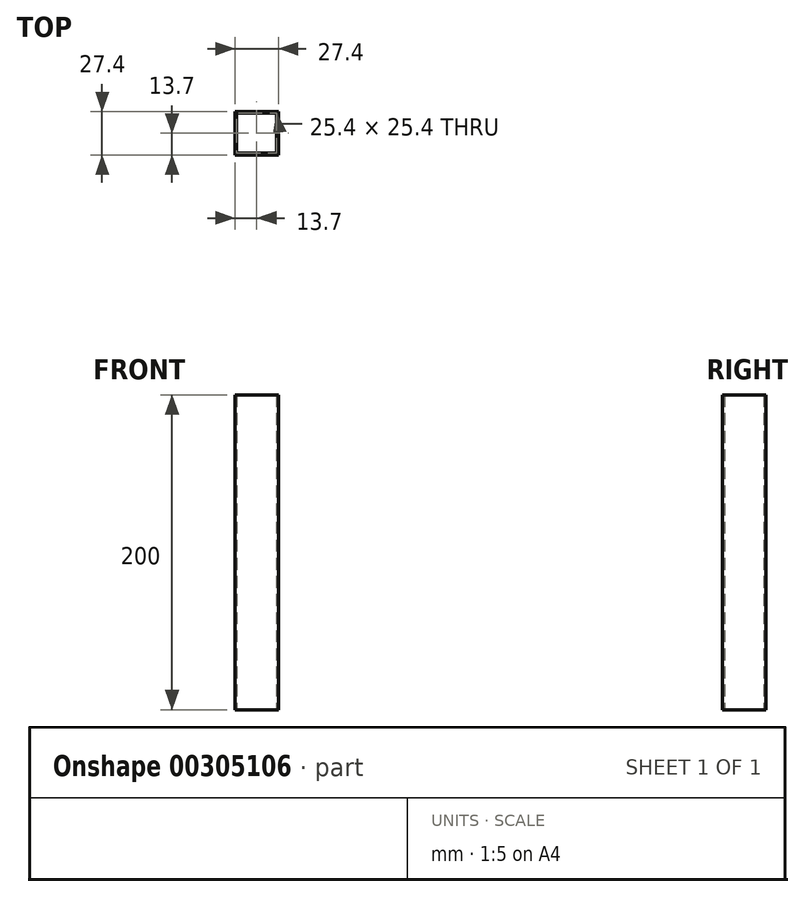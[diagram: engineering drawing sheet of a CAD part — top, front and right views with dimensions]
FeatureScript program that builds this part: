
annotation { "Feature Type Name" : "Feature", "Feature Type Description" : "" }
export const myFeature = defineFeature(function(context is Context, id is Id, definition is map)
    precondition{}
    {
        {
            var Q0;
            Q0=qCreatedBy(makeId("Top.planeOp"),FACE);
            var sketch = newSketch(context, id + "F0", { "sketchPlane" : qUnion([Q0])});
            skLineSegment(sketch, "E0.bottom", {"start": v(12.7, -12.7) * mm, "end": v(-12.7, -12.7) * mm});
            skLineSegment(sketch, "E0.top", {"start": v(12.7, 12.7) * mm, "end": v(-12.7, 12.7) * mm});
            skLineSegment(sketch, "E0.left", {"start": v(12.7, -12.7) * mm, "end": v(12.7, 12.7) * mm});
            skLineSegment(sketch, "E0.right", {"start": v(-12.7, -12.7) * mm, "end": v(-12.7, 12.7) * mm});
            skPoint(sketch, "E0.middle", {"position": v(0, 0) * mm});
            skLineSegment(sketch, "E1.bottom", {"start": v(-13.7, 13.7) * mm, "end": v(13.7, 13.7) * mm});
            skLineSegment(sketch, "E1.top", {"start": v(-13.7, -13.7) * mm, "end": v(13.7, -13.7) * mm});
            skLineSegment(sketch, "E1.left", {"start": v(-13.7, 13.7) * mm, "end": v(-13.7, -13.7) * mm});
            skLineSegment(sketch, "E1.right", {"start": v(13.7, 13.7) * mm, "end": v(13.7, -13.7) * mm});
            skSolve(sketch);
        }
        {
            var Q0;
            Q0=makeQuery(id+"F0.imprint","IMPRINT",FACE,{"disambiguationData":[TD([[makeQuery(id+"F0.imprint","IMPRINT",EDGE,{"derivedFrom":sQuery(id+"F0.wireOp",EDGE,"E0.bottom")}),1.0]])]});
            extrude(context, id + "F1", {"entities" : qUnion([Q0]), "depth" : 200 * mm, "symmetric" : true});
        }
    });
